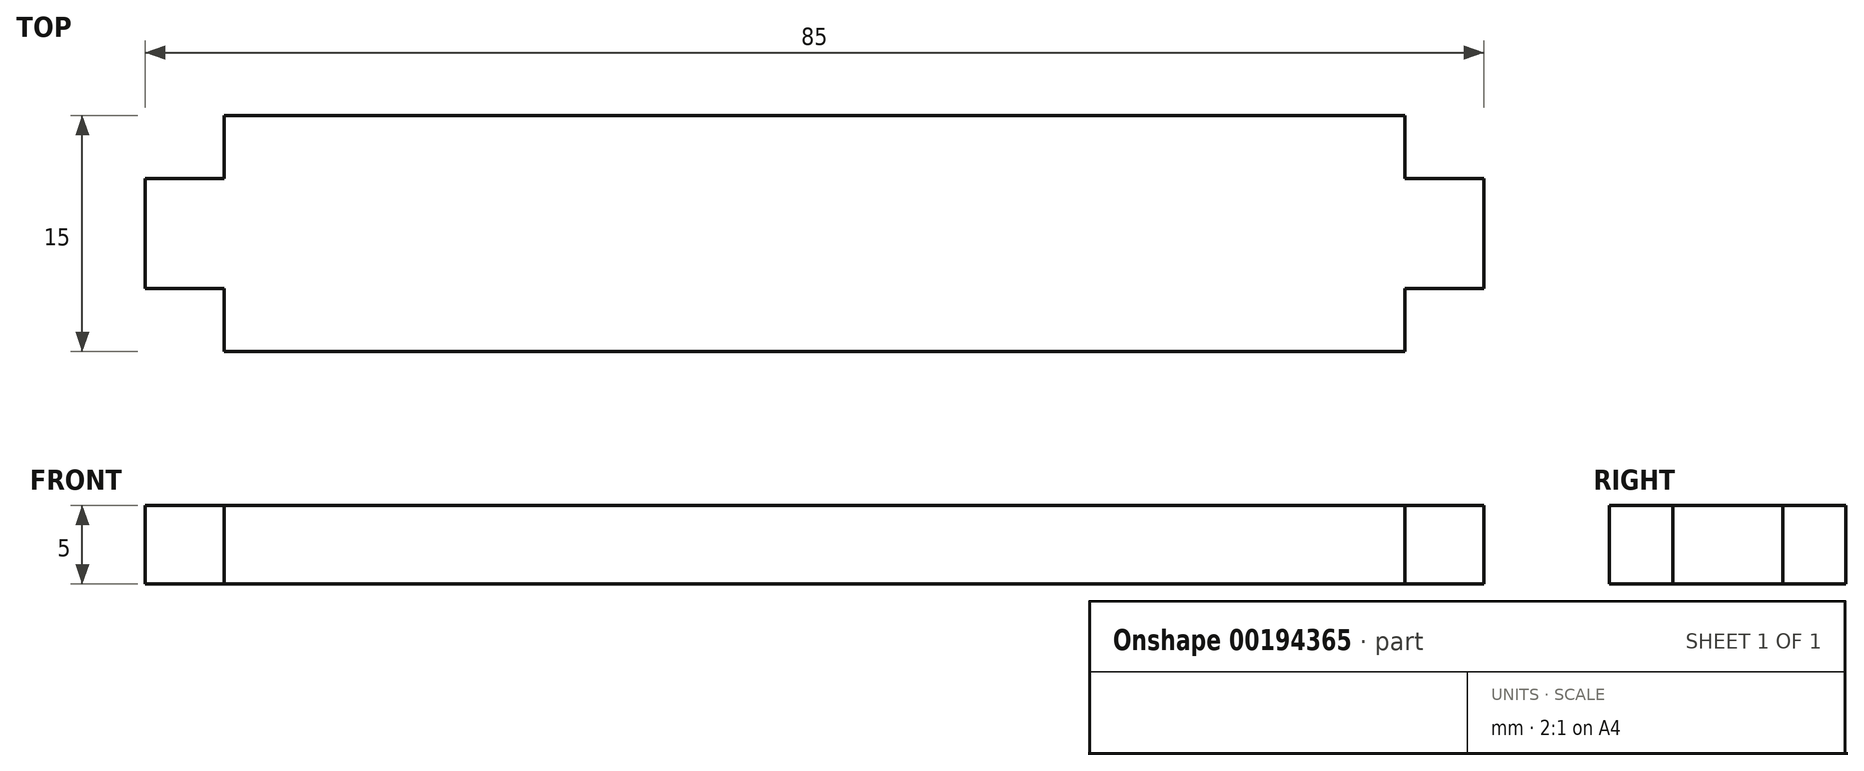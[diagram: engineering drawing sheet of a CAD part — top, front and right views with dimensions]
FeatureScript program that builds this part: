
annotation { "Feature Type Name" : "Feature", "Feature Type Description" : "" }
export const myFeature = defineFeature(function(context is Context, id is Id, definition is map)
    precondition{}
    {
        {
            var Q0;
            Q0=qCreatedBy(makeId("Top.planeOp"),FACE);
            var sketch = newSketch(context, id + "F0", { "sketchPlane" : qUnion([Q0])});
            skLineSegment(sketch, "E0.bottom", {"start": v(-37.5, -7.5) * mm, "end": v(37.5, -7.5) * mm});
            skLineSegment(sketch, "E0.top", {"start": v(-37.5, 7.5) * mm, "end": v(37.5, 7.5) * mm});
            skLineSegment(sketch, "E0.left", {"start": v(-37.5, -7.5) * mm, "end": v(-37.5, 7.5) * mm});
            skLineSegment(sketch, "E0.right", {"start": v(37.5, -7.5) * mm, "end": v(37.5, 7.5) * mm});
            skPoint(sketch, "E0.middle", {"position": v(0, 0) * mm});
            skLineSegment(sketch, "E1.bottom", {"start": v(37.5, 3.5) * mm, "end": v(42.5, 3.5) * mm});
            skLineSegment(sketch, "E1.top", {"start": v(37.5, -3.5) * mm, "end": v(42.5, -3.5) * mm});
            skLineSegment(sketch, "E1.right", {"start": v(42.5, 3.5) * mm, "end": v(42.5, -3.5) * mm});
            skLineSegment(sketch, "E2", {"start": v(42.5, 0) * mm, "end": v(37.5, 0) * mm, "construction": true});
            skLineSegment(sketch, "E3", {"start": v(0, 0) * mm, "end": v(0, 7.5) * mm, "construction": true});
            skLineSegment(sketch, "E4.MirrorCS", {"start": v(-37.5, 3.5) * mm, "end": v(-42.5, 3.5) * mm});
            skLineSegment(sketch, "E5.MirrorCS", {"start": v(-42.5, 3.5) * mm, "end": v(-42.5, -3.5) * mm});
            skLineSegment(sketch, "E6.MirrorCS", {"start": v(-37.5, -3.5) * mm, "end": v(-42.5, -3.5) * mm});
            skLineSegment(sketch, "E7.MirrorCS", {"start": v(-42.5, 0) * mm, "end": v(-37.5, 0) * mm, "construction": true});
            skSolve(sketch);
        }
        {
            var Q0;
            Q0 = qSketchRegion(id + "F0", true);
            extrude(context, id + "F1", {"entities" : qUnion([Q0]), "depth" : 5 * mm});
        }
    });
